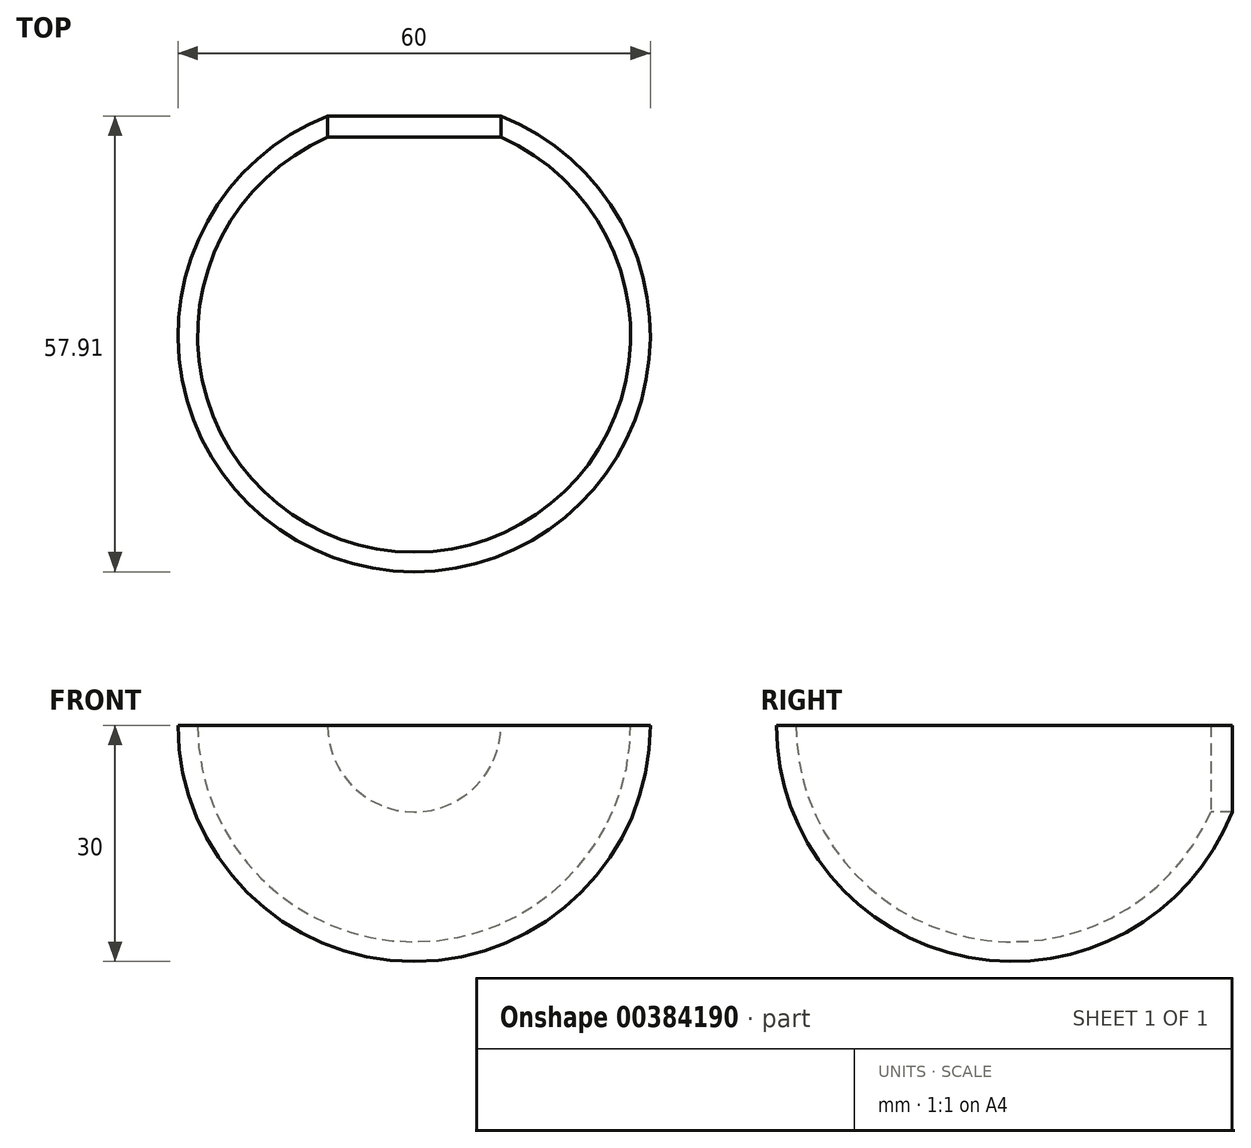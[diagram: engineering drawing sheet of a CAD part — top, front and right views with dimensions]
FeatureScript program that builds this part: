
annotation { "Feature Type Name" : "Feature", "Feature Type Description" : "" }
export const myFeature = defineFeature(function(context is Context, id is Id, definition is map)
    precondition{}
    {
        {
            var Q0;
            Q0=qCreatedBy(makeId("Top.planeOp"),FACE);
            var sketch = newSketch(context, id + "F0", { "sketchPlane" : qUnion([Q0])});
            skCircle(sketch, "E0", {"center": v(0, 0) * mm, "radius": 30 * mm});
            skLineSegment(sketch, "E1", {"start": v(0, 0) * mm, "end": v(0, 30) * mm});
            skLineSegment(sketch, "E2", {"start": v(0, 30) * mm, "end": v(0, -30) * mm});
            skCircle(sketch, "E3", {"center": v(0, 0) * mm, "radius": 27.5 * mm});
            skSolve(sketch);
        }
        {
            var Q0;
            {var subQ0=sQuery(id+"F0.wireOp",EDGE,"E2");var subQ1=sQuery(id+"F0.wireOp",EDGE,"E0");var subQ2=makeQuery(id+"F0.imprint","INTERSECT",VERTEX,{"disambiguationData":[OD(0.0)],"derivedFrom":[subQ1,subQ0]});Q0=makeQuery(id+"F0.imprint","IMPRINT",FACE,{"disambiguationData":[TD([[makeQuery(id+"F0.imprint","IMPRINT",EDGE,{"disambiguationData":[TD([[subQ2,1.0]])],"derivedFrom":subQ1}),1.0]])]});}
            var Q1;
            Q1=sQuery(id+"F0.wireOp",EDGE,"E2");
            revolve(context, id + "F1", {"entities" : qUnion([Q0]), "axis" : qUnion([Q1]), "revolveType" : RevolveType.ONE_DIRECTION, "angle" : 180 * degree});
        }
        {
            var Q0;
            Q0=qCreatedBy(makeId("Front.planeOp"),FACE);
            var sketch = newSketch(context, id + "F2", { "sketchPlane" : qUnion([Q0])});
            skPoint(sketch, "E4.0", {"position": v(0, 0) * mm});
            skCircle(sketch, "E5", {"center": v(0, 0) * mm, "radius": 11 * mm});
            skSolve(sketch);
        }
        {
            var Q0;
            Q0=makeQuery(id+"F2.imprint","IMPRINT",FACE,{"disambiguationData":[TD([[makeQuery(id+"F2.imprint","IMPRINT",EDGE,{"derivedFrom":sQuery(id+"F2.wireOp",EDGE,"E5")}),1.0]])]});
            extrude(context, id + "F3", {"entities" : qUnion([Q0]), "operationType" : NewBodyOperationType.REMOVE, "oppositeDirection" : true, "depth" : 60 * mm});
        }
    });
